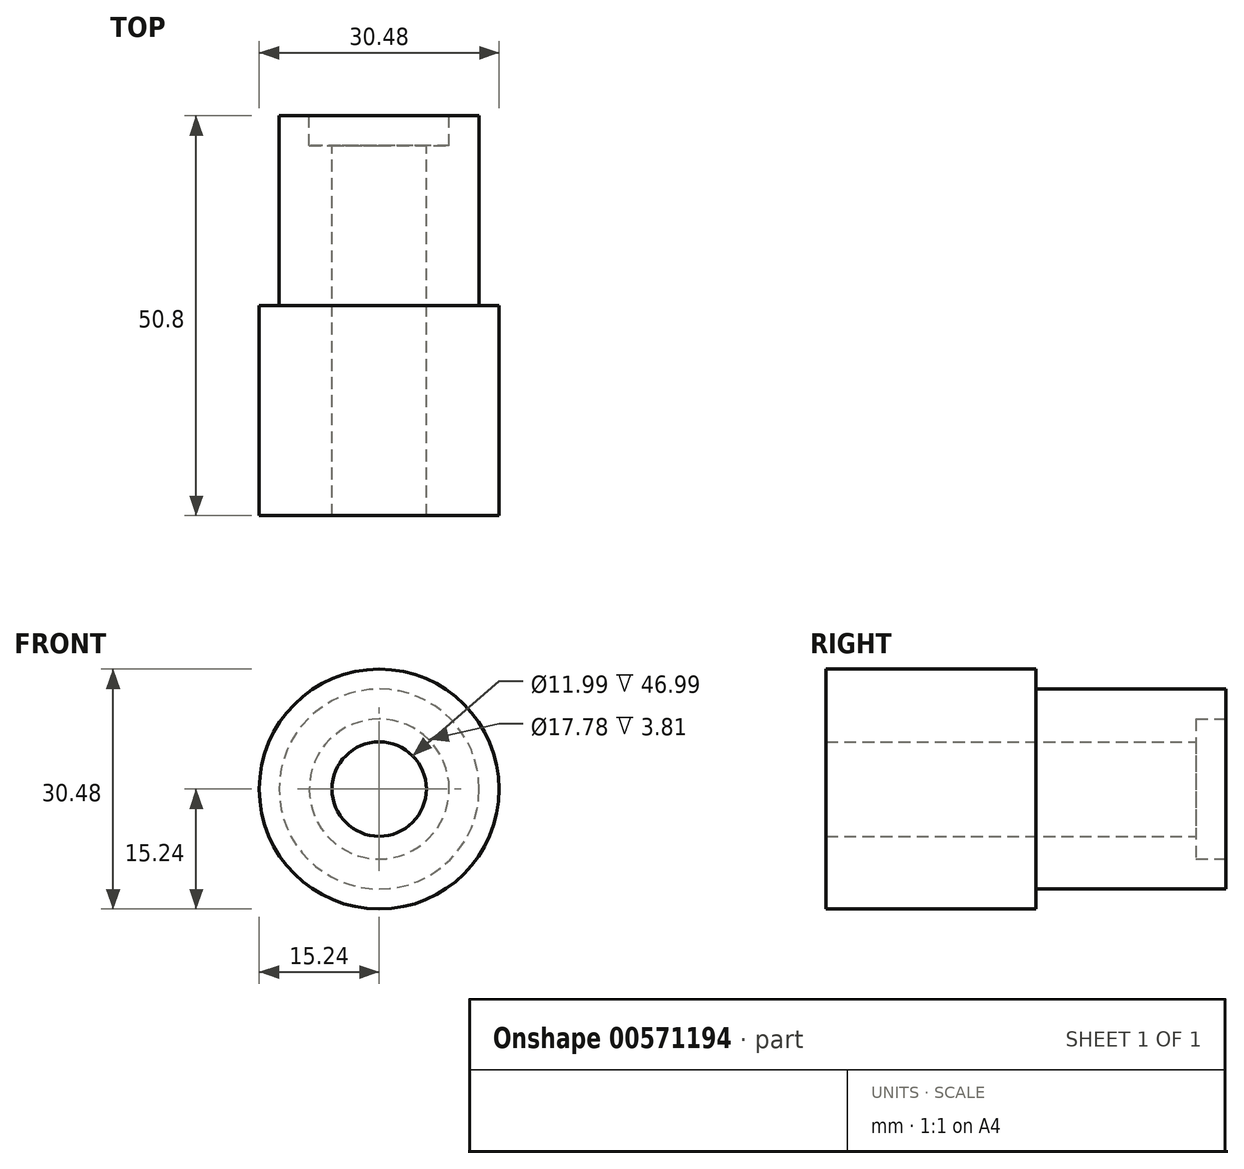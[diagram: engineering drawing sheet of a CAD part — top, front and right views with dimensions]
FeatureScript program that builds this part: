
annotation { "Feature Type Name" : "Feature", "Feature Type Description" : "" }
export const myFeature = defineFeature(function(context is Context, id is Id, definition is map)
    precondition{}
    {
        {
            var Q0;
            Q0=qCreatedBy(makeId("Front.planeOp"),FACE);
            var sketch = newSketch(context, id + "F0", { "sketchPlane" : qUnion([Q0])});
            skCircle(sketch, "E0", {"center": v(0, 0) * mm, "radius": 15.24 * mm});
            skCircle(sketch, "E1", {"center": v(0, 0) * mm, "radius": 6 * mm});
            skSolve(sketch);
        }
        {
            var Q0;
            Q0=qSketchRegion(id+"F0",true);
            extrude(context, id + "F1", {"entities" : qUnion([Q0]), "depth" : 50.8 * mm});
        }
        {
            var Q0;
            Q0=makeQuery(id+"F1.opExtrude","CAP_FACE",FACE,{"disambiguationData":[OSD([sQuery(id+"F0.wireOp",EDGE,"E0"),sQuery(id+"F0.wireOp",EDGE,"E1")])],"isStart":true});
            var sketch = newSketch(context, id + "F2", { "sketchPlane" : qUnion([Q0])});
            skCircle(sketch, "E2", {"center": v(0, 0) * mm, "radius": 12.7 * mm});
            skCircle(sketch, "E3", {"center": v(0, 0) * mm, "radius": 18.44 * mm});
            skSolve(sketch);
        }
        {
            var Q0;
            Q0=qSketchRegion(id+"F2",true);
            extrude(context, id + "F3", {"entities" : qUnion([Q0]), "operationType" : NewBodyOperationType.REMOVE, "oppositeDirection" : true, "depth" : 24.13 * mm});
        }
        {
            var Q0;
            Q0=makeQuery(id+"F1.opExtrude","CAP_FACE",FACE,{"disambiguationData":[OSD([sQuery(id+"F0.wireOp",EDGE,"E0"),sQuery(id+"F0.wireOp",EDGE,"E1")])],"isStart":true});
            var sketch = newSketch(context, id + "F4", { "sketchPlane" : qUnion([Q0])});
            skCircle(sketch, "E4", {"center": v(0, 0) * mm, "radius": 8.9 * mm});
            skSolve(sketch);
        }
        {
            var Q0;
            Q0=qSketchRegion(id+"F4",true);
            extrude(context, id + "F5", {"entities" : qUnion([Q0]), "operationType" : NewBodyOperationType.REMOVE, "oppositeDirection" : true, "depth" : 3.8 * mm});
        }
    });
